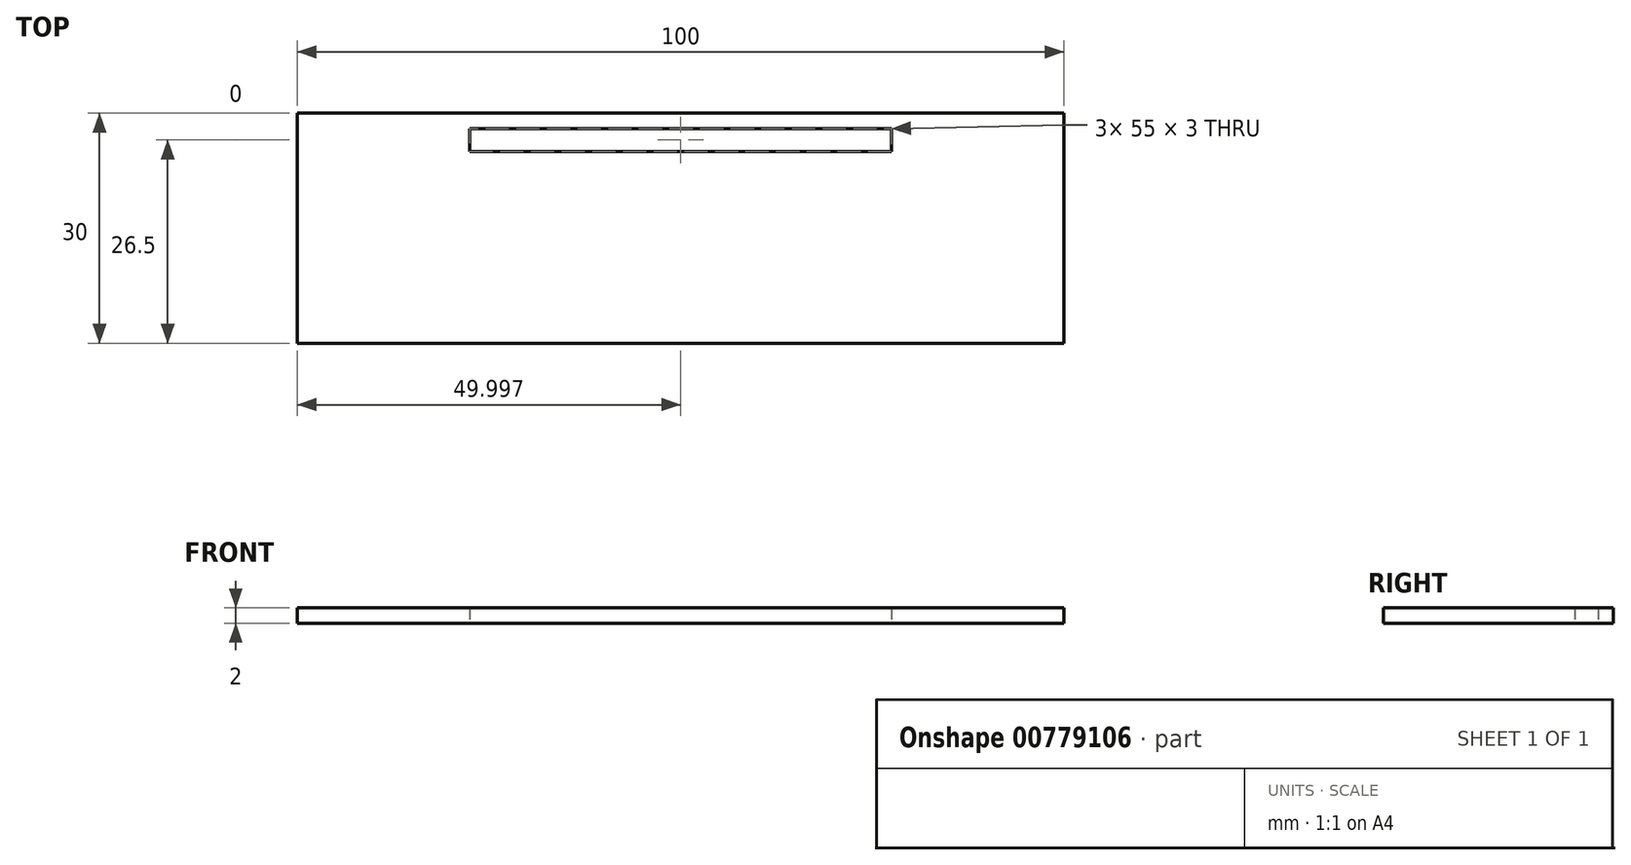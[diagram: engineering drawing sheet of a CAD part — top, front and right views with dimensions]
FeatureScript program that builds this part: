
annotation { "Feature Type Name" : "Feature", "Feature Type Description" : "" }
export const myFeature = defineFeature(function(context is Context, id is Id, definition is map)
    precondition{}
    {
        {
            var Q0;
            Q0=qCreatedBy(makeId("Top.planeOp"),FACE);
            var sketch = newSketch(context, id + "F0", { "sketchPlane" : qUnion([Q0])});
            skLineSegment(sketch, "E0.bottom", {"start": v(-64.86, 50.06) * mm, "end": v(-9.86, 50.06) * mm});
            skLineSegment(sketch, "E0.top", {"start": v(-64.86, 47.06) * mm, "end": v(-9.86, 47.06) * mm});
            skLineSegment(sketch, "E0.left", {"start": v(-64.86, 50.06) * mm, "end": v(-64.86, 47.06) * mm});
            skLineSegment(sketch, "E0.right", {"start": v(-9.86, 50.06) * mm, "end": v(-9.86, 47.06) * mm});
            skLineSegment(sketch, "E1.bottom", {"start": v(-87.36, 52.06) * mm, "end": v(12.64, 52.06) * mm});
            skLineSegment(sketch, "E1.top", {"start": v(-87.36, 22.06) * mm, "end": v(12.64, 22.06) * mm});
            skLineSegment(sketch, "E1.left", {"start": v(-87.36, 52.06) * mm, "end": v(-87.36, 22.06) * mm});
            skLineSegment(sketch, "E1.right", {"start": v(12.64, 52.06) * mm, "end": v(12.64, 22.06) * mm});
            skSolve(sketch);
        }
        {
            var Q0;
            Q0=makeQuery(id+"F0.imprint","IMPRINT",FACE,{"disambiguationData":[TD([[makeQuery(id+"F0.imprint","IMPRINT",EDGE,{"derivedFrom":sQuery(id+"F0.wireOp",EDGE,"E0.bottom")}),1.0]])]});
            extrude(context, id + "F1", {"entities" : qUnion([Q0]), "depth" : 2 * mm, "offsetDistance" : 25 * mm});
        }
    });
